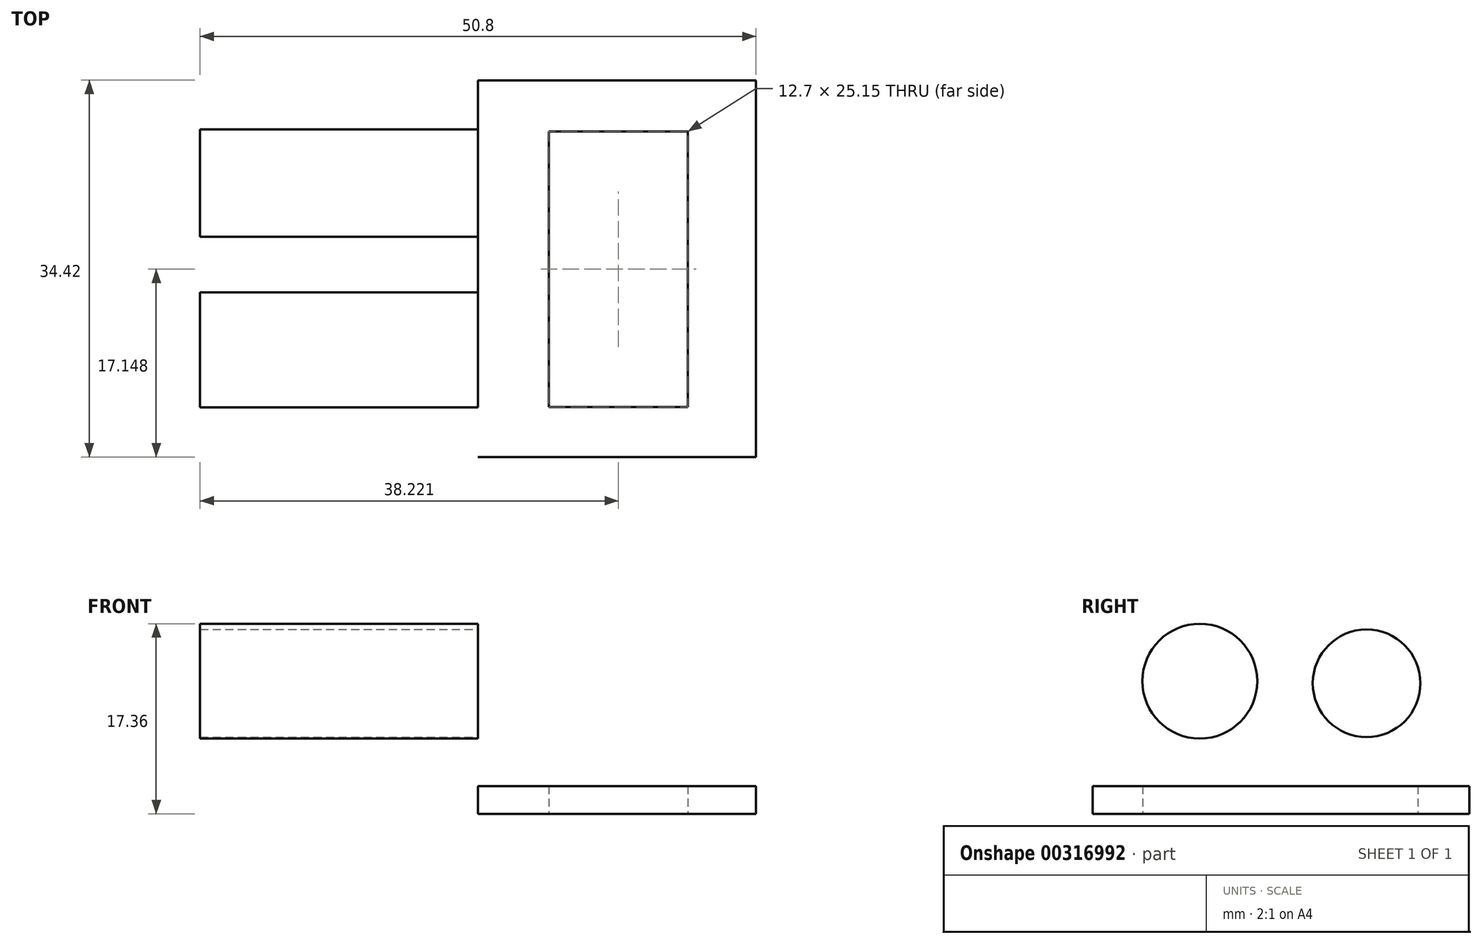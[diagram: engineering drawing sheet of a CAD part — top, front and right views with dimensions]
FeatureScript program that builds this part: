
annotation { "Feature Type Name" : "Feature", "Feature Type Description" : "" }
export const myFeature = defineFeature(function(context is Context, id is Id, definition is map)
    precondition{}
    {
        {
            var Q0;
            Q0=qCreatedBy(makeId("Top.planeOp"),FACE);
            var sketch = newSketch(context, id + "F0", { "sketchPlane" : qUnion([Q0])});
            skLineSegment(sketch, "E0.bottom", {"start": v(-6.34, 13.07) * mm, "end": v(6.36, 13.07) * mm});
            skLineSegment(sketch, "E0.top", {"start": v(-6.34, -12.09) * mm, "end": v(6.36, -12.09) * mm});
            skLineSegment(sketch, "E0.left", {"start": v(-6.34, 13.07) * mm, "end": v(-6.34, -12.09) * mm});
            skLineSegment(sketch, "E0.right", {"start": v(6.36, 13.07) * mm, "end": v(6.36, -12.09) * mm});
            skLineSegment(sketch, "E1.bottom", {"start": v(-12.8, 17.76) * mm, "end": v(12.6, 17.76) * mm});
            skLineSegment(sketch, "E1.top", {"start": v(-12.8, -16.66) * mm, "end": v(12.6, -16.66) * mm});
            skLineSegment(sketch, "E1.left", {"start": v(-12.8, 17.76) * mm, "end": v(-12.8, -16.66) * mm});
            skLineSegment(sketch, "E1.right", {"start": v(12.6, 17.76) * mm, "end": v(12.6, -16.66) * mm});
            skSolve(sketch);
        }
        {
            var Q0;
            Q0 = qSketchRegion(id + "F0", true);
            extrude(context, id + "F1", {"entities" : qUnion([Q0]), "depth" : 2.54 * mm});
        }
        {
            var Q0;
            Q0=makeQuery(id+"F1.opExtrude","SWEPT_FACE",FACE,{"disambiguationData":[OSD([sQuery(id+"F0.wireOp",EDGE,"E1.left")])]});
            var sketch = newSketch(context, id + "F2", { "sketchPlane" : qUnion([Q0])});
            skCircle(sketch, "E2", {"center": v(6.88, 12.12) * mm, "radius": 5.25 * mm});
            skCircle(sketch, "E3", {"center": v(-8.36, 11.92) * mm, "radius": 4.92 * mm});
            skSolve(sketch);
        }
        {
            var Q0;
            Q0=makeQuery(id+"F2.imprint","IMPRINT",FACE,{"disambiguationData":[TD([[makeQuery(id+"F2.imprint","IMPRINT",EDGE,{"derivedFrom":sQuery(id+"F2.wireOp",EDGE,"E3")}),1.0]])]});
            var Q1;
            Q1=makeQuery(id+"F2.imprint","IMPRINT",FACE,{"disambiguationData":[TD([[makeQuery(id+"F2.imprint","IMPRINT",EDGE,{"derivedFrom":sQuery(id+"F2.wireOp",EDGE,"E2")}),1.0]])]});
            extrude(context, id + "F3", {"entities" : qUnion([Q0, Q1]), "operationType" : NewBodyOperationType.ADD, "depth" : 25.4 * mm});
        }
    });
